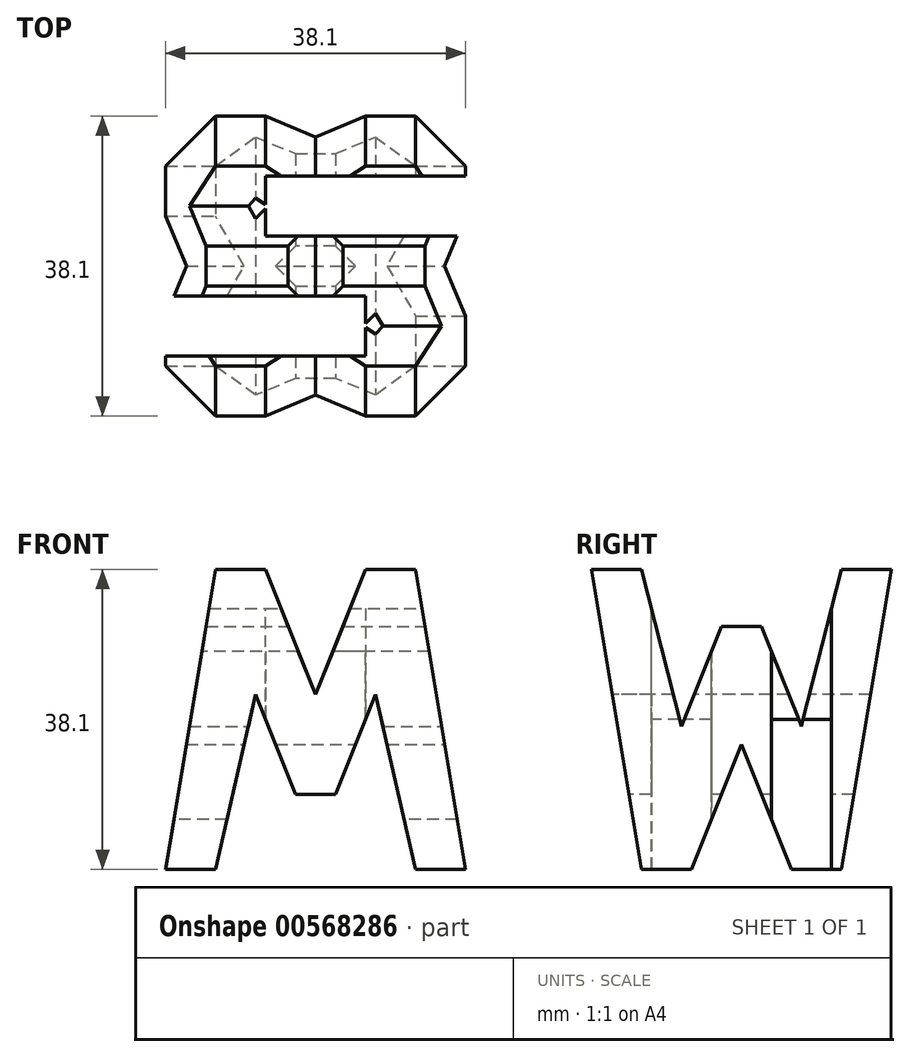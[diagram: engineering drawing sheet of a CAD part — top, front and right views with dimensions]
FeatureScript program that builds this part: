
annotation { "Feature Type Name" : "Feature", "Feature Type Description" : "" }
export const myFeature = defineFeature(function(context is Context, id is Id, definition is map)
    precondition{}
    {
        {
            var Q0;
            Q0=qCreatedBy(makeId("Front.planeOp"),FACE);
            var sketch = newSketch(context, id + "F0", { "sketchPlane" : qUnion([Q0])});
            skLineSegment(sketch, "E0", {"start": v(0, 0) * mm, "end": v(38.1, 0) * mm});
            skLineSegment(sketch, "E1", {"start": v(38.1, 0) * mm, "end": v(38.1, 38.1) * mm});
            skLineSegment(sketch, "E2", {"start": v(38.1, 38.1) * mm, "end": v(0, 38.1) * mm});
            skLineSegment(sketch, "E3", {"start": v(0, 38.1) * mm, "end": v(0, 0) * mm});
            skSolve(sketch);
        }
        {
            var Q0;
            Q0=qSketchRegion(id+"F0",true);
            extrude(context, id + "F1", {"entities" : qUnion([Q0]), "depth" : 38.1 * mm});
        }
        {
            var Q0;
            Q0=qCreatedBy(makeId("Front.planeOp"),FACE);
            cPlane(context, id + "F2", {"entities" : qUnion([Q0]), "cplaneType" : CPlaneType.OFFSET, "offset" : 38.1 * mm, "width" : 152.4 * mm, "height" : 152.4 * mm});
        }
        {
            var Q0;
            Q0=qCreatedBy(makeId("Right.planeOp"),FACE);
            cPlane(context, id + "F3", {"entities" : qUnion([Q0]), "cplaneType" : CPlaneType.OFFSET, "offset" : 38.1 * mm, "width" : 152.4 * mm, "height" : 152.4 * mm});
        }
        {
            var Q0;
            Q0=qCreatedBy(makeId("Top.planeOp"),FACE);
            cPlane(context, id + "F4", {"entities" : qUnion([Q0]), "cplaneType" : CPlaneType.OFFSET, "offset" : 38.1 * mm, "width" : 152.4 * mm, "height" : 152.4 * mm});
        }
        {
            var Q0;
            Q0=qCreatedBy(id+"F3.planeOp",FACE);
            var sketch = newSketch(context, id + "F5", { "sketchPlane" : qUnion([Q0])});
            skLineSegment(sketch, "E4", {"start": v(0, 0) * mm, "end": v(0, 38.1) * mm});
            skLineSegment(sketch, "E5", {"start": v(0, 38.1) * mm, "end": v(-38.1, 38.1) * mm});
            skLineSegment(sketch, "E6", {"start": v(-38.1, 38.1) * mm, "end": v(-38.1, 0) * mm});
            skLineSegment(sketch, "E7", {"start": v(-38.1, 0) * mm, "end": v(0, 0) * mm});
            skLineSegment(sketch, "E8", {"start": v(-38.1, 38.1) * mm, "end": v(-31.75, 0) * mm});
            skLineSegment(sketch, "E9", {"start": v(-31.75, 0) * mm, "end": v(-25.4, 0) * mm});
            skLineSegment(sketch, "E10", {"start": v(-25.4, 0) * mm, "end": v(-19.05, 15.88) * mm});
            skLineSegment(sketch, "E11", {"start": v(-19.05, 15.88) * mm, "end": v(-12.7, 0) * mm});
            skLineSegment(sketch, "E12", {"start": v(-12.7, 0) * mm, "end": v(-6.35, 0) * mm});
            skLineSegment(sketch, "E13", {"start": v(-6.35, 0) * mm, "end": v(0, 38.1) * mm});
            skLineSegment(sketch, "E14", {"start": v(-31.75, 38.1) * mm, "end": v(-26.67, 18.2) * mm});
            skLineSegment(sketch, "E15", {"start": v(-26.67, 18.2) * mm, "end": v(-21.59, 30.9) * mm});
            skLineSegment(sketch, "E16", {"start": v(-21.59, 30.9) * mm, "end": v(-16.51, 30.9) * mm});
            skLineSegment(sketch, "E17", {"start": v(-16.51, 30.9) * mm, "end": v(-11.43, 18.2) * mm});
            skLineSegment(sketch, "E18", {"start": v(-11.43, 18.2) * mm, "end": v(-6.35, 38.1) * mm});
            skSolve(sketch);
        }
        {
            var Q0;
            {var subQ0=sQuery(id+"F5.wireOp",EDGE,"E6");Q0=makeQuery(id+"F5.imprint","IMPRINT",FACE,{"disambiguationData":[TD([[makeQuery(id+"F5.imprint","IMPRINT",EDGE,{"derivedFrom":subQ0}),1.0]])]});}
            var Q1;
            {var subQ0=sQuery(id+"F5.wireOp",EDGE,"E14");Q1=makeQuery(id+"F5.imprint","IMPRINT",FACE,{"disambiguationData":[TD([[makeQuery(id+"F5.imprint","IMPRINT",EDGE,{"derivedFrom":subQ0}),1.0]])]});}
            var Q2;
            {var subQ0=sQuery(id+"F5.wireOp",EDGE,"E10");Q2=makeQuery(id+"F5.imprint","IMPRINT",FACE,{"disambiguationData":[TD([[makeQuery(id+"F5.imprint","IMPRINT",EDGE,{"derivedFrom":subQ0}),-1.0]])]});}
            var Q3;
            {var subQ0=sQuery(id+"F5.wireOp",EDGE,"E4");Q3=makeQuery(id+"F5.imprint","IMPRINT",FACE,{"disambiguationData":[TD([[makeQuery(id+"F5.imprint","IMPRINT",EDGE,{"derivedFrom":subQ0}),1.0]])]});}
            extrude(context, id + "F6", {"entities" : qUnion([Q0, Q1, Q2, Q3]), "operationType" : NewBodyOperationType.REMOVE, "oppositeDirection" : true, "depth" : 38.1 * mm});
        }
        {
            var Q0;
            Q0=qCreatedBy(id+"F2.planeOp",FACE);
            var sketch = newSketch(context, id + "F7", { "sketchPlane" : qUnion([Q0])});
            skLineSegment(sketch, "E19", {"start": v(0, 0) * mm, "end": v(0, 38.1) * mm});
            skLineSegment(sketch, "E20", {"start": v(0, 38.1) * mm, "end": v(38.1, 38.1) * mm});
            skLineSegment(sketch, "E21", {"start": v(38.1, 38.1) * mm, "end": v(38.1, 0) * mm});
            skLineSegment(sketch, "E22", {"start": v(38.1, 0) * mm, "end": v(0, 0) * mm});
            skLineSegment(sketch, "E23", {"start": v(0, 0) * mm, "end": v(6.35, 38.1) * mm});
            skLineSegment(sketch, "E24", {"start": v(6.35, 38.1) * mm, "end": v(12.7, 38.1) * mm});
            skLineSegment(sketch, "E25", {"start": v(12.7, 38.1) * mm, "end": v(19.05, 22.22) * mm});
            skLineSegment(sketch, "E26", {"start": v(19.05, 22.23) * mm, "end": v(25.4, 38.1) * mm});
            skLineSegment(sketch, "E27", {"start": v(25.4, 38.1) * mm, "end": v(31.75, 38.1) * mm});
            skLineSegment(sketch, "E28", {"start": v(31.75, 38.1) * mm, "end": v(38.1, 0) * mm});
            skLineSegment(sketch, "E29", {"start": v(31.75, 0) * mm, "end": v(26.67, 22.23) * mm});
            skLineSegment(sketch, "E30", {"start": v(26.67, 22.23) * mm, "end": v(21.59, 9.52) * mm});
            skLineSegment(sketch, "E31", {"start": v(21.59, 9.53) * mm, "end": v(16.51, 9.53) * mm});
            skLineSegment(sketch, "E32", {"start": v(16.51, 9.52) * mm, "end": v(11.43, 22.23) * mm});
            skLineSegment(sketch, "E33", {"start": v(11.43, 22.23) * mm, "end": v(6.35, 0) * mm});
            skLineSegment(sketch, "E34", {"start": v(6.35, 0) * mm, "end": v(0, 0) * mm});
            skSolve(sketch);
        }
        {
            var Q0;
            {var subQ0=sQuery(id+"F7.wireOp",EDGE,"E19");Q0=makeQuery(id+"F7.imprint","IMPRINT",FACE,{"disambiguationData":[TD([[makeQuery(id+"F7.imprint","IMPRINT",EDGE,{"derivedFrom":subQ0}),-1.0]])]});}
            var Q1;
            {var subQ0=sQuery(id+"F7.wireOp",EDGE,"E25");Q1=makeQuery(id+"F7.imprint","IMPRINT",FACE,{"disambiguationData":[TD([[makeQuery(id+"F7.imprint","IMPRINT",EDGE,{"derivedFrom":subQ0}),1.0]])]});}
            var Q2;
            {var subQ0=sQuery(id+"F7.wireOp",EDGE,"E21");Q2=makeQuery(id+"F7.imprint","IMPRINT",FACE,{"disambiguationData":[TD([[makeQuery(id+"F7.imprint","IMPRINT",EDGE,{"derivedFrom":subQ0}),-1.0]])]});}
            var Q3;
            {var subQ0=sQuery(id+"F7.wireOp",EDGE,"E29");Q3=makeQuery(id+"F7.imprint","IMPRINT",FACE,{"disambiguationData":[TD([[makeQuery(id+"F7.imprint","IMPRINT",EDGE,{"derivedFrom":subQ0}),1.0]])]});}
            extrude(context, id + "F8", {"entities" : qUnion([Q0, Q1, Q2, Q3]), "operationType" : NewBodyOperationType.REMOVE, "oppositeDirection" : true, "depth" : 38.1 * mm});
        }
        {
            var Q0;
            Q0=qCreatedBy(id+"F4.planeOp",FACE);
            var sketch = newSketch(context, id + "F9", { "sketchPlane" : qUnion([Q0])});
            skLineSegment(sketch, "E35", {"start": v(0, 0) * mm, "end": v(0, -38.1) * mm});
            skLineSegment(sketch, "E36", {"start": v(0, -38.1) * mm, "end": v(38.1, -38.1) * mm});
            skLineSegment(sketch, "E37", {"start": v(38.1, -38.1) * mm, "end": v(38.1, 0) * mm});
            skLineSegment(sketch, "E38", {"start": v(38.1, 0) * mm, "end": v(0, 0) * mm});
            skLineSegment(sketch, "E39", {"start": v(38.1, -7.62) * mm, "end": v(12.7, -7.62) * mm});
            skLineSegment(sketch, "E40", {"start": v(12.7, -7.62) * mm, "end": v(12.7, -15.24) * mm});
            skLineSegment(sketch, "E41", {"start": v(12.7, -15.24) * mm, "end": v(38.1, -15.24) * mm});
            skLineSegment(sketch, "E42", {"start": v(0, -22.86) * mm, "end": v(25.4, -22.86) * mm});
            skLineSegment(sketch, "E43", {"start": v(25.4, -22.86) * mm, "end": v(25.4, -30.48) * mm});
            skLineSegment(sketch, "E44", {"start": v(25.4, -30.48) * mm, "end": v(0, -30.48) * mm});
            skSolve(sketch);
        }
        {
            var Q0;
            {var subQ0=sQuery(id+"F9.wireOp",EDGE,"E42");Q0=makeQuery(id+"F9.imprint","IMPRINT",FACE,{"disambiguationData":[TD([[makeQuery(id+"F9.imprint","IMPRINT",EDGE,{"derivedFrom":subQ0}),-1.0]])]});}
            var Q1;
            {var subQ0=sQuery(id+"F9.wireOp",EDGE,"E39");Q1=makeQuery(id+"F9.imprint","IMPRINT",FACE,{"disambiguationData":[TD([[makeQuery(id+"F9.imprint","IMPRINT",EDGE,{"derivedFrom":subQ0}),1.0]])]});}
            extrude(context, id + "F10", {"entities" : qUnion([Q0, Q1]), "operationType" : NewBodyOperationType.REMOVE, "oppositeDirection" : true, "depth" : 38.1 * mm});
        }
    });
